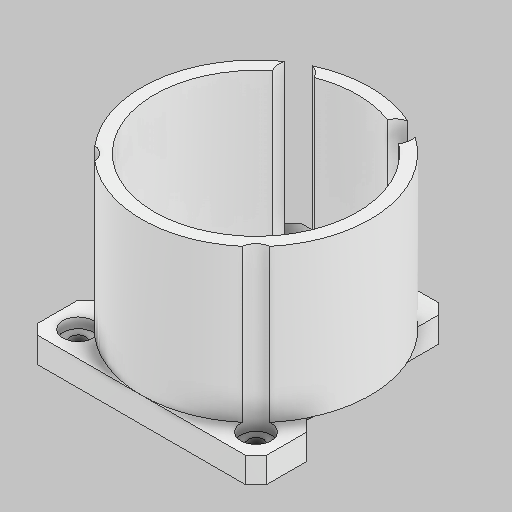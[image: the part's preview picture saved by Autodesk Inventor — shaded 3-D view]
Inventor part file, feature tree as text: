
AUTODESK INVENTOR PART (.ipt)
format: ipt  version: 2025.2 (Build 292293000, 293)  size: 357,888 bytes
history: native  units: in
note: dims shown in document units (in); Inventor stores cm internally (conversion verified against a paired STEP export)
features: extrude x4, sketch x4, chamfer x2
ambient origin geometry x8: Origin, YZ Plane, XZ Plane, XY Plane, X Axis, Y Axis, Z Axis, Center Point
bodies: Solid1 (feature_tree)
feature tree (10):
  extrude  "Extrusion1"  Depth=1.7717in
  chamfer  "Chamfer1"  Distance=0.1969in
  chamfer  "Chamfer2"  Distance=0.1969in
  extrude  "Extrusion5"  Depth=0.1969in
  extrude  "Extrusion6"  Depth=0.1969in
  extrude  "Extrusion7"  Depth=0.1181in
  sketch  "Sketch1"  dims[d0=1.7717in d1=1.7717in]
  sketch  "Sketch5"  dims[d2=0.1181in]
  sketch  "Sketch6"  dims[d3=0.1181in]
  sketch  "Sketch7"  dims[d4=1.378in d5=0.1969in d6=0.1969in d7=0.1969in d8=0.1969in d9=0.1181in d10=0.1181in d11=0.7874in d12=0.1969in d13=0.1969in d14=0.3937in d15=0.6102in d16=0.6299in d17=0.3937in d18=0.3937in d19=0.2756in d20=0.2756in d21=0.1181in d22=0.0in d23=0.0787in d24=0.0787in d25=45.0deg d26=0.2756in d27=0.2756in d28=0.2756in d29=0.0787in d30=45.0deg d59=0.2362in d60=0.2362in d61=0.2362in d62=0.2362in d63=0.0787in d64=0.0in d65=1.5748in d66=1.1811in d67=0.0in d68=0.9449in d69=0.374in d70=0.748in d71=0.0787in d72=0.0in]
